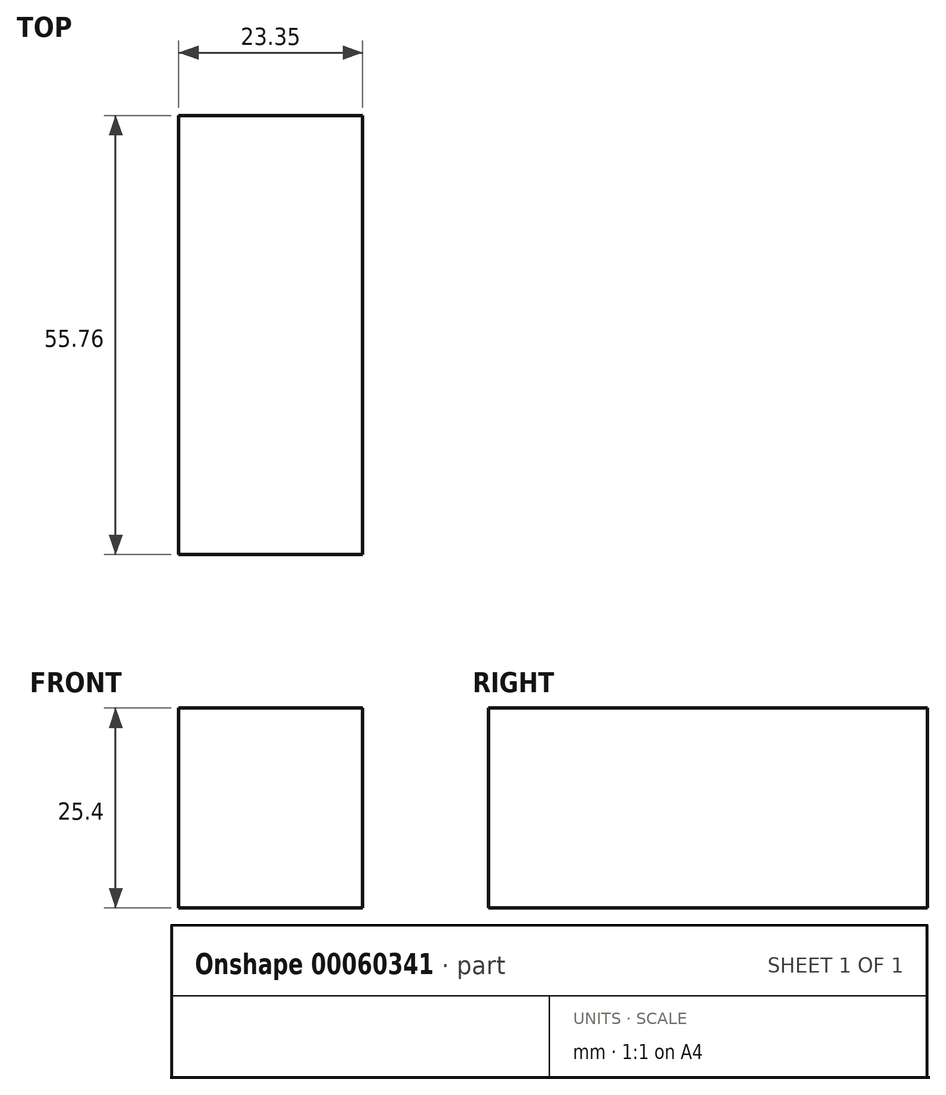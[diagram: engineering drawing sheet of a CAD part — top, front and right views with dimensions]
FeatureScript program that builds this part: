
annotation { "Feature Type Name" : "Feature", "Feature Type Description" : "" }
export const myFeature = defineFeature(function(context is Context, id is Id, definition is map)
    precondition{}
    {
        {
            var Q0;
            Q0=qCreatedBy(makeId("Top.planeOp"),FACE);
            var sketch = newSketch(context, id + "F0", { "sketchPlane" : qUnion([Q0])});
            skLineSegment(sketch, "E0.bottom", {"start": v(0, -41.91) * mm, "end": v(23.35, -41.91) * mm});
            skLineSegment(sketch, "E0.top", {"start": v(0, 13.85) * mm, "end": v(23.35, 13.85) * mm});
            skLineSegment(sketch, "E0.left", {"start": v(0, -41.91) * mm, "end": v(0, 13.85) * mm});
            skLineSegment(sketch, "E0.right", {"start": v(23.35, -41.91) * mm, "end": v(23.35, 13.85) * mm});
            skSolve(sketch);
        }
        {
            var Q0;
            Q0=makeQuery(id+"F0.imprint","IMPRINT",FACE,{"disambiguationData":[TD([[makeQuery(id+"F0.imprint","IMPRINT",EDGE,{"derivedFrom":sQuery(id+"F0.wireOp",EDGE,"E0.bottom")}),1.0]])]});
            extrude(context, id + "F1", {"entities" : qUnion([Q0]), "depth" : 25.4 * mm});
        }
    });
